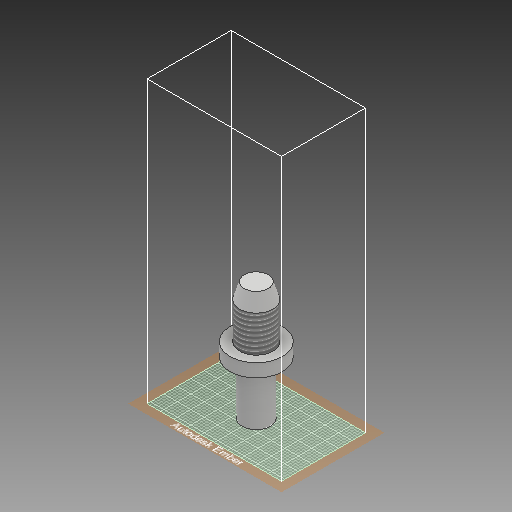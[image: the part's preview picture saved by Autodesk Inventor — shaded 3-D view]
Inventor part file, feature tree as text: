
AUTODESK INVENTOR PART (.ipt)
format: ipt  version: 2018 (Build 220112000, 112)  size: 570,880 bytes
history: native  units: in
note: dims shown in document units (in); Inventor stores cm internally (conversion verified against a paired STEP export)
features: sketch x8, extrude x3, plane x2, other x2, loft x1, helix x1
ambient origin geometry x8: Origin, YZ Plane, XZ Plane, XY Plane, X Axis, Y Axis, Z Axis, Center Point
bodies: Body1 (feature_tree)
feature tree (17):
  extrude  "Extrusion2"  Depth=0.2462in TaperAngle=0.0deg
  extrude  "Extrusion3"  Depth=1.0in TaperAngle=0.0deg
  extrude  "Extrusion4"  Depth=0.6821in TaperAngle=0.0deg
  plane  "Work Plane1"
  loft  "Loft1"
  sketch  "Sketch9"  dims[d23=0.08in d24=1.0in d25=3.189in d26=0.0in d27=90.0deg d28=90.0deg d29=0.0in d30=0.0in]
  other  "Work Axis1"
  sketch  "3D Sketch3"
  sketch  "3D Sketch4"
  plane  "Work Plane5"
  helix  "Coil1"  [1 undecoded]
  sketch  "Sketch3"  dims[d4=0.9781in d5=0.2462in d6=0.0in]
  sketch  "Sketch4"  dims[d7=0.5274in d8=1.0in d9=0.0in]
  sketch  "Sketch5"  dims[d10=0.6258in d11=0.6821in d12=0.0in]
  sketch  "Sketch7"  dims[d15=0.2899in d16=0.0in d17=90.0deg d18=0.0in d19=90.0deg]
  other  "Edges1"
  sketch  "Sketch14"
note: 1 required parameter value undecoded (feature->parameter linkage not recoverable at this tier; creation-order binding heuristic only, values carry confidence <= 0.55)
